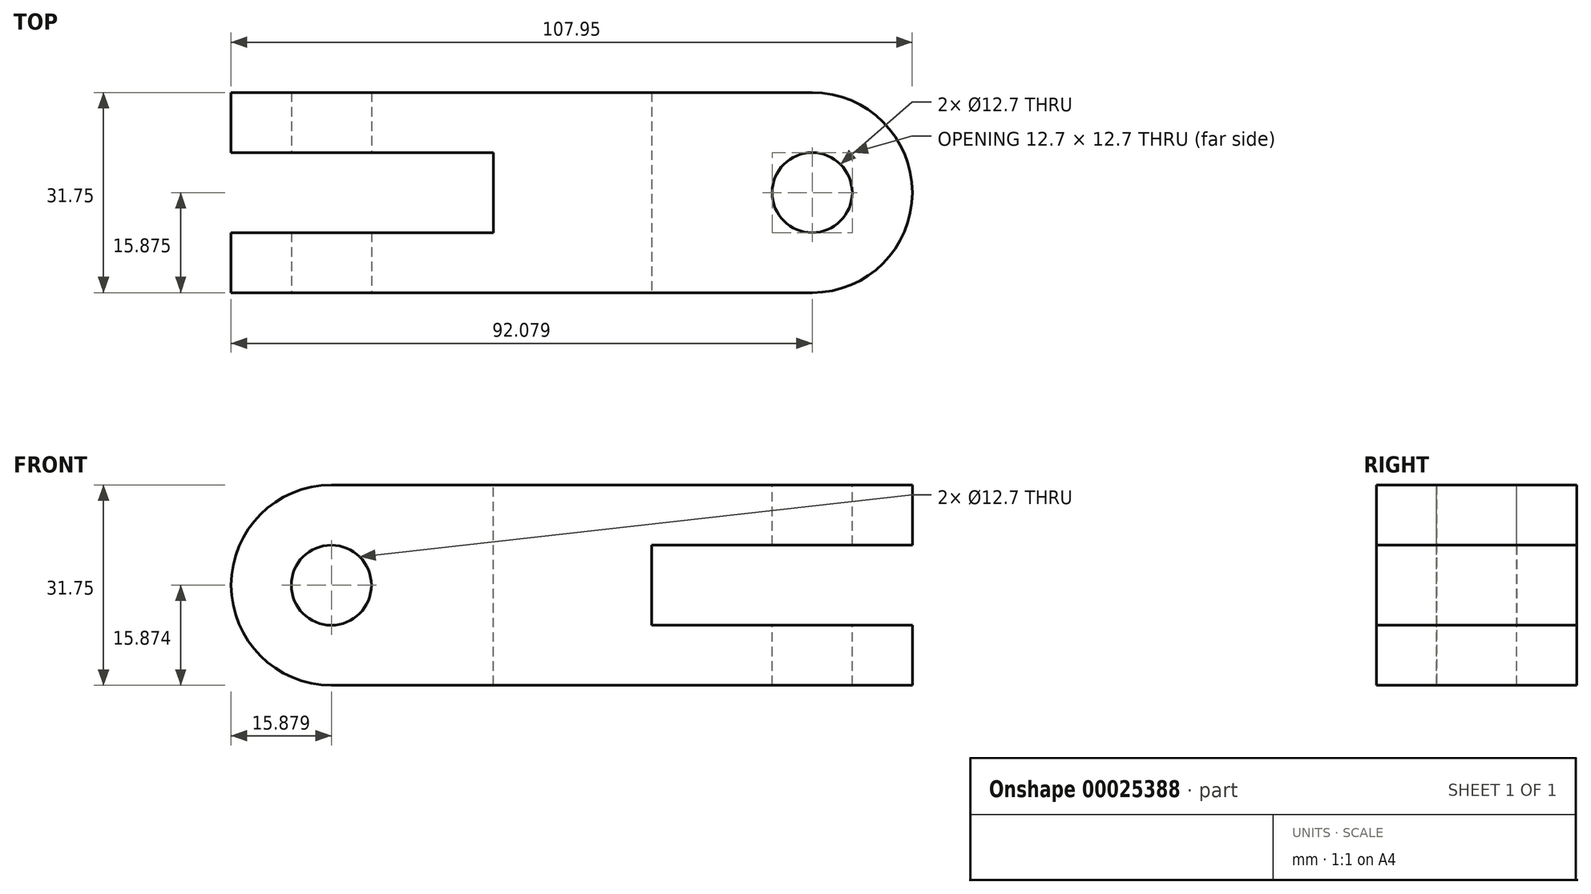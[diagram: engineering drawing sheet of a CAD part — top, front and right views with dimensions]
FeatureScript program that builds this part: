
annotation { "Feature Type Name" : "Feature", "Feature Type Description" : "" }
export const myFeature = defineFeature(function(context is Context, id is Id, definition is map)
    precondition{}
    {
        {
            var Q0;
            Q0=qCreatedBy(makeId("Front.planeOp"),FACE);
            var sketch = newSketch(context, id + "F0", { "sketchPlane" : qUnion([Q0])});
            skLineSegment(sketch, "E0.bottom", {"start": v(-49.26, -13.81) * mm, "end": v(58.7, -13.81) * mm});
            skLineSegment(sketch, "E0.top", {"start": v(-49.26, -45.56) * mm, "end": v(58.7, -45.56) * mm});
            skLineSegment(sketch, "E0.left", {"start": v(-49.26, -13.81) * mm, "end": v(-49.26, -45.56) * mm});
            skLineSegment(sketch, "E0.right", {"start": v(58.7, -13.81) * mm, "end": v(58.7, -45.56) * mm});
            skSolve(sketch);
        }
        {
            var Q0;
            Q0 = qSketchRegion(id + "F0", true);
            extrude(context, id + "F1", {"entities" : qUnion([Q0]), "depth" : 31.75 * mm});
        }
        {
            var Q0;
            Q0=makeQuery(id+"F1.opExtrude","CAP_FACE",FACE,{"disambiguationData":[OSD([sQuery(id+"F0.wireOp",EDGE,"E0.bottom"),sQuery(id+"F0.wireOp",EDGE,"E0.top"),sQuery(id+"F0.wireOp",EDGE,"E0.left"),sQuery(id+"F0.wireOp",EDGE,"E0.right")])],"isStart":false});
            var sketch = newSketch(context, id + "F2", { "sketchPlane" : qUnion([Q0])});
            skLineSegment(sketch, "E1.0", {"start": v(17.42, -23.34) * mm, "end": v(17.42, -36.04) * mm});
            skArc(sketch, "E2", {"start": v(-33.38, -13.81) * mm, "mid": v(-49.26, -29.69) * mm, "end": v(-33.38, -45.56) * mm});
            skCircle(sketch, "E3", {"center": v(-33.38, -29.69) * mm, "radius": 6.35 * mm});
            skLineSegment(sketch, "E4.trimOffspring", {"start": v(17.42, -23.34) * mm, "end": v(58.7, -23.34) * mm});
            skLineSegment(sketch, "E5.trimOffspring", {"start": v(17.42, -36.04) * mm, "end": v(58.7, -36.04) * mm});
            skSolve(sketch);
        }
        {
            var Q0;
            {var subQ0=sQuery(id+"F2.wireOp",EDGE,"E3");var subQ1=sQuery(id+"F2.wireOp",EDGE,"16585ff5-e809-4fb9-aace-63a6c38cd7ac.0");var subQ3=makeQuery(id+"F2.imprint","INTERSECT",VERTEX,{"disambiguationData":[OD(0.0)],"derivedFrom":[subQ1,subQ0]});Q0=makeQuery(id+"F2.imprint","IMPRINT",FACE,{"disambiguationData":[TD([[makeQuery(id+"F2.imprint","IMPRINT",EDGE,{"disambiguationData":[TD([[subQ3,-1.0]])],"derivedFrom":subQ1}),1.0]])]});}
            var Q1;
            {var subQ0=makeQuery(id+"F1.opExtrude","CAP_EDGE",EDGE,{"disambiguationData":[OSD([sQuery(id+"F0.wireOp",EDGE,"E0.left")])],"isStart":false});var subQ3=makeQuery(id+"F1.opExtrude","CAP_EDGE",EDGE,{"disambiguationData":[OSD([sQuery(id+"F0.wireOp",EDGE,"E0.bottom")])],"isStart":false});var subQ4=makeQuery(id+"F2.imprint","INTERSECT",VERTEX,{"derivedFrom":[subQ3,subQ0]});Q1=makeQuery(id+"F2.imprint","IMPRINT",FACE,{"disambiguationData":[TD([[makeQuery(id+"F2.imprint","IMPRINT",EDGE,{"disambiguationData":[TD([[subQ4,-1.0]])],"derivedFrom":subQ0}),1.0]])]});}
            var Q2;
            {var subQ0=makeQuery(id+"F1.opExtrude","CAP_EDGE",EDGE,{"disambiguationData":[OSD([sQuery(id+"F0.wireOp",EDGE,"E0.left")])],"isStart":false});var subQ3=makeQuery(id+"F1.opExtrude","CAP_EDGE",EDGE,{"disambiguationData":[OSD([sQuery(id+"F0.wireOp",EDGE,"E0.top")])],"isStart":false});var subQ4=makeQuery(id+"F2.imprint","INTERSECT",VERTEX,{"derivedFrom":[subQ3,subQ0]});Q2=makeQuery(id+"F2.imprint","IMPRINT",FACE,{"disambiguationData":[TD([[makeQuery(id+"F2.imprint","IMPRINT",EDGE,{"disambiguationData":[TD([[subQ4,1.0]])],"derivedFrom":subQ0}),1.0]])]});}
            var Q3;
            Q3=makeQuery(id+"F2.imprint","IMPRINT",FACE,{"disambiguationData":[TD([[makeQuery(id+"F2.imprint","IMPRINT",EDGE,{"derivedFrom":sQuery(id+"F2.wireOp",EDGE,"E1.0")}),1.0]])]});
            var Q4;
            Q4=makeQuery(id+"F2.imprint","IMPRINT",FACE,{"disambiguationData":[TD([[makeQuery(id+"F2.imprint","IMPRINT",EDGE,{"derivedFrom":sQuery(id+"F2.wireOp",EDGE,"E3")}),1.0]])]});
            extrude(context, id + "F3", {"entities" : qUnion([Q0, Q1, Q2, Q3, Q4]), "operationType" : NewBodyOperationType.REMOVE, "endBound" : BoundingType.THROUGH_ALL, "oppositeDirection" : true, "depth" : 25.4 * mm});
        }
        {
            var Q0;
            Q0=makeQuery(id+"F1.opExtrude","SWEPT_FACE",FACE,{"disambiguationData":[OSD([sQuery(id+"F0.wireOp",EDGE,"E0.bottom")])]});
            var sketch = newSketch(context, id + "F4", { "sketchPlane" : qUnion([Q0])});
            skLineSegment(sketch, "E6.0", {"start": v(-49.26, -31.75) * mm, "end": v(-49.26, 0) * mm});
            skLineSegment(sketch, "E7", {"start": v(58.7, 0) * mm, "end": v(-49.26, 0) * mm});
            skLineSegment(sketch, "E8", {"start": v(-49.26, -31.75) * mm, "end": v(58.7, -31.75) * mm});
            skLineSegment(sketch, "E9.0", {"start": v(-49.26, -22.23) * mm, "end": v(-7.73, -22.23) * mm});
            skArc(sketch, "E10", {"start": v(42.82, -31.75) * mm, "mid": v(58.7, -15.88) * mm, "end": v(42.82, 0) * mm});
            skCircle(sketch, "E11", {"center": v(42.82, -15.88) * mm, "radius": 6.35 * mm});
            skLineSegment(sketch, "E12.0", {"start": v(-7.73, -22.23) * mm, "end": v(-7.73, -9.52) * mm});
            skLineSegment(sketch, "E13.trimOffspring", {"start": v(-7.73, -9.53) * mm, "end": v(-49.26, -9.53) * mm});
            skSolve(sketch);
        }
        {
            var Q0;
            {var subQ1=sQuery(id+"F4.wireOp",EDGE,"E10");var subQ3=sQuery(id+"F4.wireOp",EDGE,"E7");var subQ5=makeQuery(id+"F4.imprint","INTERSECT",VERTEX,{"derivedFrom":[subQ3,subQ1]});Q0=makeQuery(id+"F4.imprint","IMPRINT",FACE,{"disambiguationData":[TD([[makeQuery(id+"F4.imprint","IMPRINT",EDGE,{"disambiguationData":[TD([[subQ5,-1.0]])],"derivedFrom":subQ3}),-1.0]])]});}
            var Q1;
            {var subQ5=sQuery(id+"F4.wireOp",EDGE,"E12.0");Q1=makeQuery(id+"F4.imprint","IMPRINT",FACE,{"disambiguationData":[TD([[makeQuery(id+"F4.imprint","IMPRINT",EDGE,{"derivedFrom":subQ5}),1.0]])]});}
            var Q2;
            {var subQ3=sQuery(id+"F4.wireOp",EDGE,"E9.0");var subQ5=sQuery(id+"F4.wireOp",EDGE,"E6.0");var subQ7=makeQuery(id+"F4.imprint","INTERSECT",VERTEX,{"derivedFrom":[subQ5,subQ3]});Q2=makeQuery(id+"F4.imprint","IMPRINT",FACE,{"disambiguationData":[TD([[makeQuery(id+"F4.imprint","IMPRINT",EDGE,{"disambiguationData":[TD([[subQ7,-1.0]])],"derivedFrom":subQ5}),-1.0]])]});}
            var Q3;
            {var subQ1=sQuery(id+"F4.wireOp",EDGE,"E10");var subQ3=sQuery(id+"F4.wireOp",EDGE,"E8");var subQ5=makeQuery(id+"F4.imprint","INTERSECT",VERTEX,{"derivedFrom":[subQ3,subQ1]});Q3=makeQuery(id+"F4.imprint","IMPRINT",FACE,{"disambiguationData":[TD([[makeQuery(id+"F4.imprint","IMPRINT",EDGE,{"disambiguationData":[TD([[subQ5,-1.0]])],"derivedFrom":subQ3}),1.0]])]});}
            var Q4;
            Q4=makeQuery(id+"F4.imprint","IMPRINT",FACE,{"disambiguationData":[TD([[makeQuery(id+"F4.imprint","IMPRINT",EDGE,{"derivedFrom":sQuery(id+"F4.wireOp",EDGE,"E11")}),1.0]])]});
            extrude(context, id + "F5", {"entities" : qUnion([Q0, Q1, Q2, Q3, Q4]), "operationType" : NewBodyOperationType.REMOVE, "endBound" : BoundingType.THROUGH_ALL, "oppositeDirection" : true, "depth" : 25.4 * mm});
        }
    });
